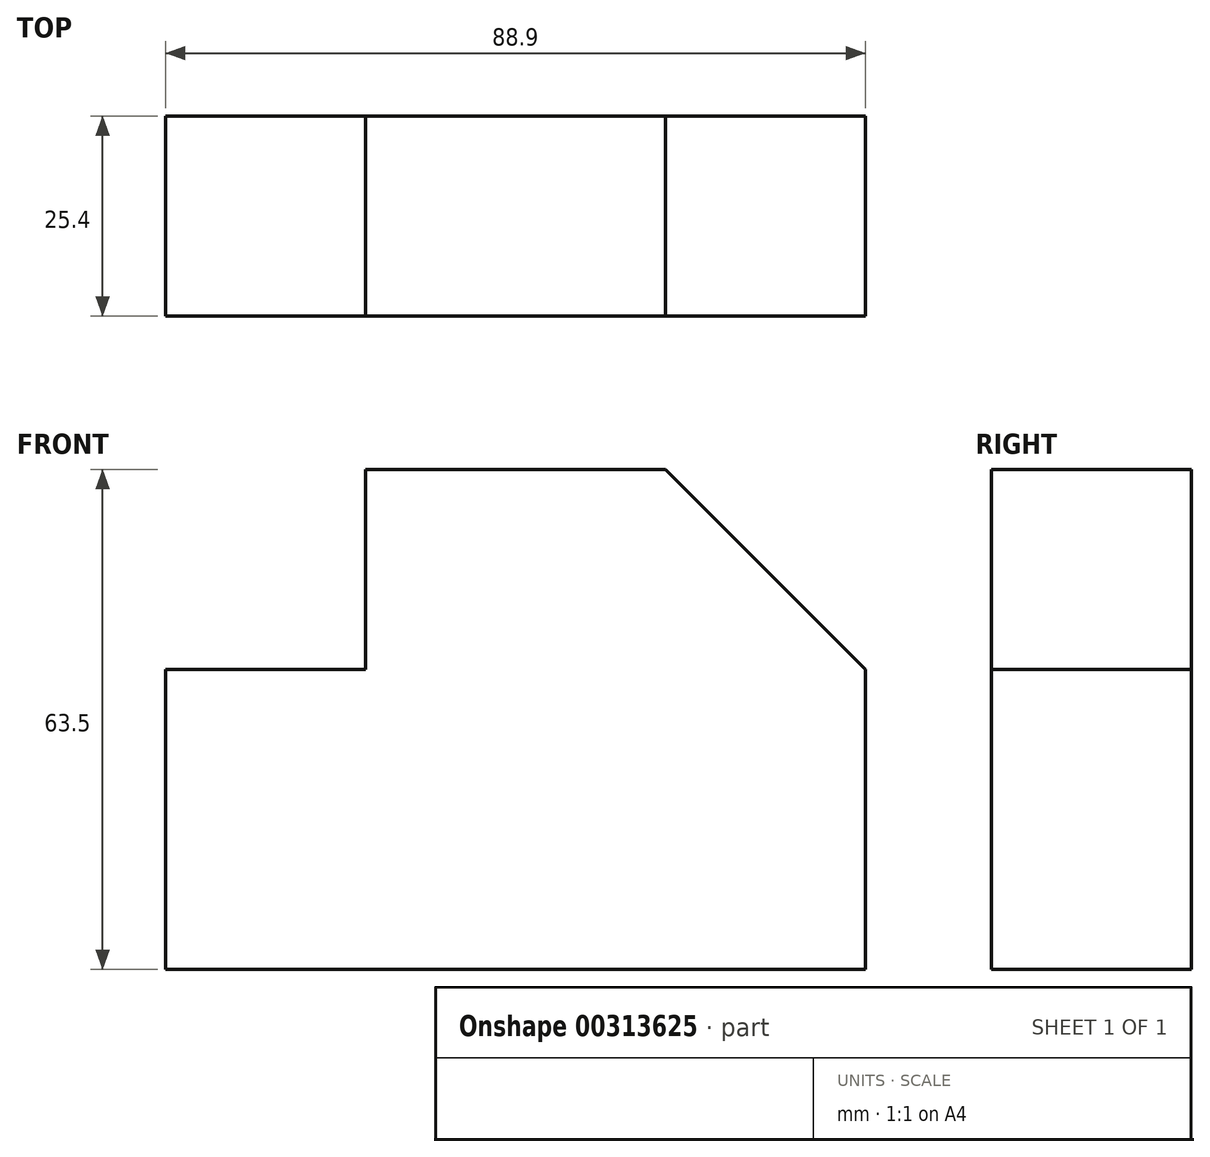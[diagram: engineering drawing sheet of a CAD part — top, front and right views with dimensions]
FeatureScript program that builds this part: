
annotation { "Feature Type Name" : "Feature", "Feature Type Description" : "" }
export const myFeature = defineFeature(function(context is Context, id is Id, definition is map)
    precondition{}
    {
        {
            var Q0;
            Q0=qCreatedBy(makeId("Front.planeOp"),FACE);
            var sketch = newSketch(context, id + "F0", { "sketchPlane" : qUnion([Q0])});
            skLineSegment(sketch, "E0", {"start": v(-47.7, -55.54) * mm, "end": v(41.2, -55.54) * mm});
            skLineSegment(sketch, "E1", {"start": v(-47.7, -55.54) * mm, "end": v(-47.7, -17.44) * mm});
            skLineSegment(sketch, "E2", {"start": v(-47.7, -17.44) * mm, "end": v(-22.3, -17.44) * mm});
            skLineSegment(sketch, "E3", {"start": v(-22.3, -17.44) * mm, "end": v(-22.3, 7.96) * mm});
            skLineSegment(sketch, "E4", {"start": v(-22.3, 7.96) * mm, "end": v(15.8, 7.96) * mm});
            skLineSegment(sketch, "E5", {"start": v(41.2, -55.54) * mm, "end": v(41.2, -17.44) * mm});
            skLineSegment(sketch, "E6", {"start": v(15.8, 7.96) * mm, "end": v(41.2, -17.44) * mm});
            skSolve(sketch);
        }
        {
            var Q0;
            Q0=makeQuery(id+"F0.imprint","IMPRINT",FACE,{"disambiguationData":[TD([[makeQuery(id+"F0.imprint","IMPRINT",EDGE,{"derivedFrom":sQuery(id+"F0.wireOp",EDGE,"E0")}),1.0]])]});
            extrude(context, id + "F1", {"entities" : qUnion([Q0]), "depth" : 25.4 * mm});
        }
    });
